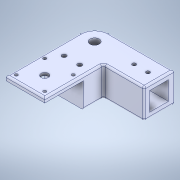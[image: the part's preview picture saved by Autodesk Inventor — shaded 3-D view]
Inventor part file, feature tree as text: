
AUTODESK INVENTOR PART (.ipt)
format: ipt  version: 2020 (Build 240168000, 168)  size: 168,448 bytes
history: imported  units: in
note: dims shown in document units (in); Inventor stores cm internally (conversion verified against a paired STEP export)
features: sketch x1, other x1, imported_body x1
ambient origin geometry x8: Origin, YZ Plane, XZ Plane, XY Plane, X Axis, Y Axis, Z Axis, Center Point
bodies: Solid1 (imported_parasolid)
feature tree (3):
  sketch  "Sketch1"
  other  "Cut-Extrude11"
  imported_body  NMx_Import_Brep_tag  [imported B-rep: ~49 faces, bbox_mm=[86.2, 32.4, 96.21]]
